# Revit family: Faucet-Kitchen-KOHLER-Barossa-K-R776_1
name_source: partatom
category: Plumbing Fixtures
revit_build: Autodesk Revit 2015 (Build: 20140606_1530(x64)
units: mm (PartAtom-declared; Revit-internal decimal feet)

## types (1)
- VS-Vibrant Stainless
    ADA Compliant = Yes
    Assembly Code = D2010
    CW Connection = Yes
    Cold Water Inlet = Cold Water Inlet
    Date Modified = 3/06/2019
    Default Elevation = 36"
    Description = Pull-down kitchen sink faucet with soap/lotion dispenser
    Drain Included = No
    Faucet Hole Spacing = 0"
    Finish = Kohler-Metal-VS-Vibrant_Stainless
    Flow Rate = 2 GPM
    HW Connection = Yes
    Handle Clearance = 0"
    Height = 15 1/2"
    Hot Water Inlet = Hot Water Inlet
    Length = 9"
    Manufacturer = KOHLER Co.
    MasterFormat 1995 = 15410
    MasterFormat 2004 = 22.41.39
    Material = Metal Construction
    Model = K-R776-SD-VS
    Pressure = 60.00 psi
    Product Documentation Link = https://www.us.kohler.com
    Product Name = Barossa
    Product Page URL = http://www.us.kohler.com
    Spout Reach = 9"
    URL = https://www.us.kohler.com
    Vent Connection = No
    Waste Connection = No
    Waste Water Outlet = Waste Water Outlet
    WaterSense Certified = No
    Width = 10 1/2"

## geometry (parser evidence)
native form markers: Sweep x9
no freeform markers — native parametric forms only
